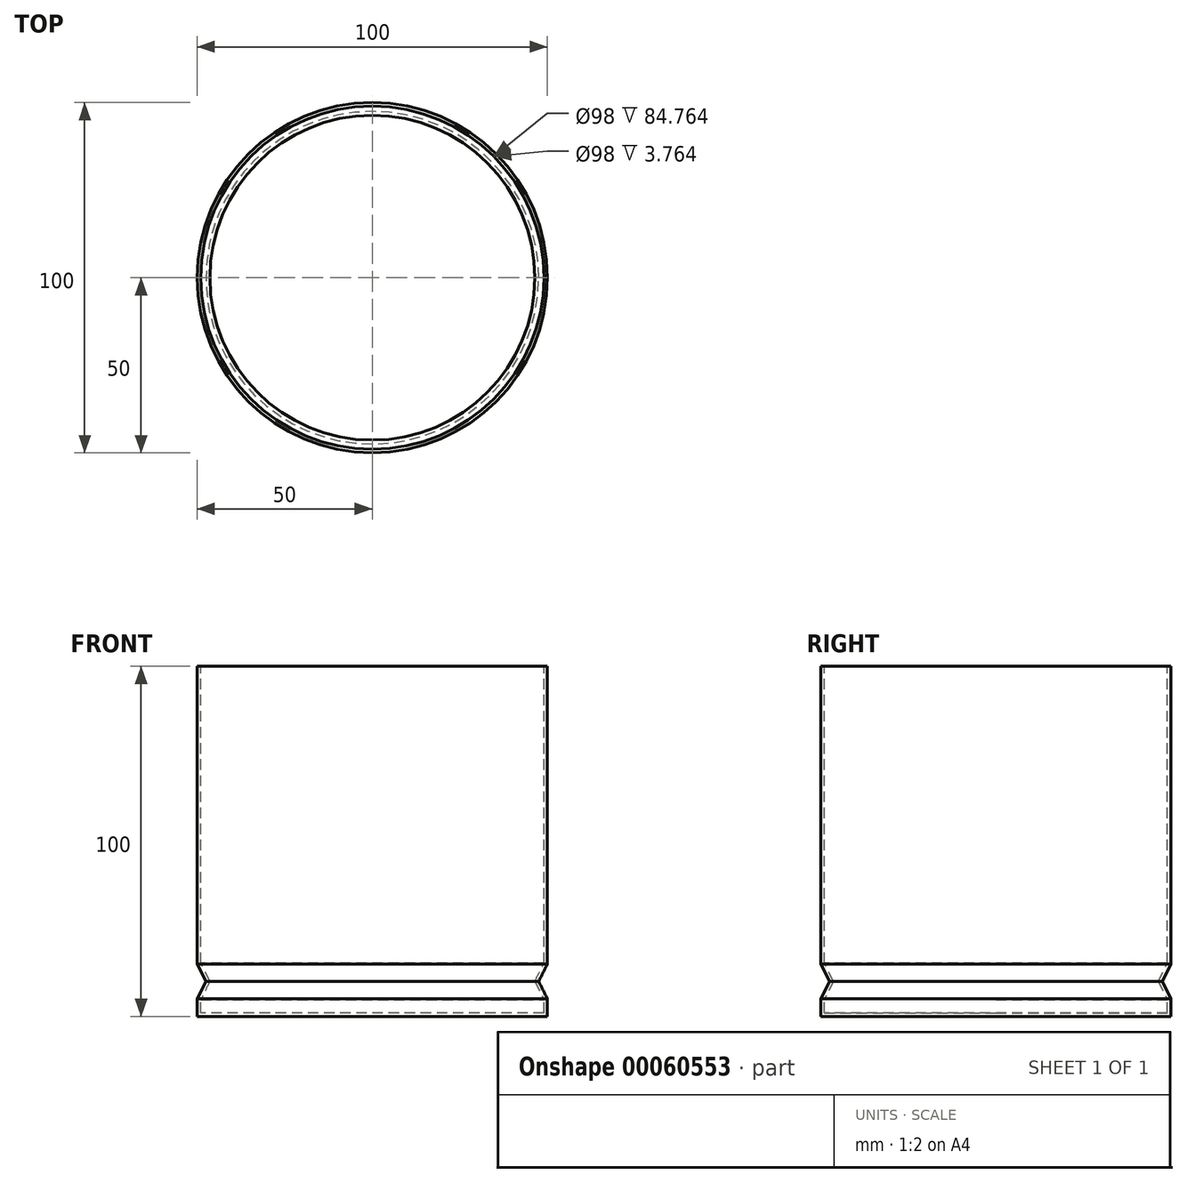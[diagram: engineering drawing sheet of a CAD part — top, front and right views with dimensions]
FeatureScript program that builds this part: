
annotation { "Feature Type Name" : "Feature", "Feature Type Description" : "" }
export const myFeature = defineFeature(function(context is Context, id is Id, definition is map)
    precondition{}
    {
        {
            var Q0;
            Q0=qCreatedBy(makeId("Top.planeOp"),FACE);
            cPlane(context, id + "F0", {"entities" : qUnion([Q0]), "cplaneType" : CPlaneType.OFFSET, "offset" : 50 * mm, "width" : 150 * mm, "height" : 150 * mm});
        }
        {
            var Q0;
            Q0=qCreatedBy(makeId("Top.planeOp"),FACE);
            cPlane(context, id + "F1", {"entities" : qUnion([Q0]), "cplaneType" : CPlaneType.OFFSET, "offset" : 35 * mm, "oppositeDirection" : true, "width" : 150 * mm, "height" : 150 * mm});
        }
        {
            var Q0;
            Q0=qCreatedBy(makeId("Top.planeOp"),FACE);
            cPlane(context, id + "F2", {"entities" : qUnion([Q0]), "cplaneType" : CPlaneType.OFFSET, "offset" : 40 * mm, "oppositeDirection" : true, "width" : 150 * mm, "height" : 150 * mm});
        }
        {
            var Q0;
            Q0=qCreatedBy(makeId("Top.planeOp"),FACE);
            cPlane(context, id + "F3", {"entities" : qUnion([Q0]), "cplaneType" : CPlaneType.OFFSET, "offset" : 45 * mm, "oppositeDirection" : true, "width" : 150 * mm, "height" : 150 * mm});
        }
        {
            var Q0;
            Q0=qCreatedBy(makeId("Top.planeOp"),FACE);
            cPlane(context, id + "F4", {"entities" : qUnion([Q0]), "cplaneType" : CPlaneType.OFFSET, "offset" : 50 * mm, "oppositeDirection" : true, "width" : 150 * mm, "height" : 150 * mm});
        }
        {
            var Q0;
            Q0=qCreatedBy(id+"F0.planeOp",FACE);
            var sketch = newSketch(context, id + "F5", { "sketchPlane" : qUnion([Q0])});
            skCircle(sketch, "E0", {"center": v(0, 0) * mm, "radius": 50 * mm});
            skSolve(sketch);
        }
        {
            var Q0;
            Q0=qCreatedBy(id+"F4.planeOp",FACE);
            var sketch = newSketch(context, id + "F6", { "sketchPlane" : qUnion([Q0])});
            skPoint(sketch, "E1.rect.middle", {"position": v(0, 0) * mm});
            skPoint(sketch, "E2.visualSharp", {"position": v(-35.36, 35.36) * mm});
            skPoint(sketch, "E3.visualSharp", {"position": v(35.36, 35.36) * mm});
            skPoint(sketch, "E4.visualSharp", {"position": v(35.36, -35.36) * mm});
            skPoint(sketch, "E5.visualSharp", {"position": v(-35.36, -35.36) * mm});
            skCircle(sketch, "E6", {"center": v(0, 0) * mm, "radius": 50 * mm});
            skSolve(sketch);
        }
        {
            var Q0;
            Q0=qCreatedBy(id+"F3.planeOp",FACE);
            var sketch = newSketch(context, id + "F7", { "sketchPlane" : qUnion([Q0])});
            skCircle(sketch, "E7", {"center": v(0, 0) * mm, "radius": 50 * mm});
            skSolve(sketch);
        }
        {
            var Q0;
            Q0=qCreatedBy(id+"F2.planeOp",FACE);
            var sketch = newSketch(context, id + "F8", { "sketchPlane" : qUnion([Q0])});
            skCircle(sketch, "E8", {"center": v(0, 0) * mm, "radius": 47.5 * mm});
            skSolve(sketch);
        }
        {
            var Q0;
            Q0=qCreatedBy(id+"F1.planeOp",FACE);
            var sketch = newSketch(context, id + "F9", { "sketchPlane" : qUnion([Q0])});
            skCircle(sketch, "E9", {"center": v(0, 0) * mm, "radius": 50 * mm});
            skSolve(sketch);
        }
        {
            var Q0;
            Q0=makeQuery(id+"F5.imprint","IMPRINT",FACE,{"disambiguationData":[TD([[makeQuery(id+"F5.imprint","IMPRINT",EDGE,{"derivedFrom":sQuery(id+"F5.wireOp",EDGE,"E0")}),1.0]])]});
            var Q1;
            Q1=makeQuery(id+"F9.imprint","IMPRINT",FACE,{"disambiguationData":[TD([[makeQuery(id+"F9.imprint","IMPRINT",EDGE,{"derivedFrom":sQuery(id+"F9.wireOp",EDGE,"E9")}),1.0]])]});
            loft(context, id + "F10", {"sheetProfilesArray" : [{ "sheetProfileEntities" : qUnion([Q0]) }, { "sheetProfileEntities" : qUnion([Q1]) }]});
        }
        {
            var Q1;
            Q1=makeQuery(id+"F10.opLoft","CAP_FACE",FACE,{"disambiguationData":[OSD([makeQuery(id+"F9.imprint","IMPRINT",FACE,{"disambiguationData":[TD([[makeQuery(id+"F9.imprint","IMPRINT",EDGE,{"derivedFrom":sQuery(id+"F9.wireOp",EDGE,"E9")}),1.0]])]})])],"isStart":true});
            var Q2;
            Q2=makeQuery(id+"F8.imprint","IMPRINT",FACE,{"disambiguationData":[TD([[makeQuery(id+"F8.imprint","IMPRINT",EDGE,{"derivedFrom":sQuery(id+"F8.wireOp",EDGE,"E8")}),1.0]])]});
            loft(context, id + "F11", {"operationType" : NewBodyOperationType.ADD, "sheetProfilesArray" : [{ "sheetProfileEntities" : qUnion([Q1]) }, { "sheetProfileEntities" : qUnion([Q2]) }]});
        }
        {
            var Q1;
            Q1=makeQuery(id+"F11.opLoft","CAP_FACE",FACE,{"disambiguationData":[OSD([makeQuery(id+"F8.imprint","IMPRINT",FACE,{"disambiguationData":[TD([[makeQuery(id+"F8.imprint","IMPRINT",EDGE,{"derivedFrom":sQuery(id+"F8.wireOp",EDGE,"E8")}),1.0]])]})])],"isStart":true});
            var Q2;
            Q2=makeQuery(id+"F7.imprint","IMPRINT",FACE,{"disambiguationData":[TD([[makeQuery(id+"F7.imprint","IMPRINT",EDGE,{"derivedFrom":sQuery(id+"F7.wireOp",EDGE,"E7")}),1.0]])]});
            loft(context, id + "F12", {"operationType" : NewBodyOperationType.ADD, "sheetProfilesArray" : [{ "sheetProfileEntities" : qUnion([Q1]) }, { "sheetProfileEntities" : qUnion([Q2]) }]});
        }
        {
            var Q1;
            Q1=makeQuery(id+"F12.opLoft","CAP_FACE",FACE,{"disambiguationData":[OSD([makeQuery(id+"F7.imprint","IMPRINT",FACE,{"disambiguationData":[TD([[makeQuery(id+"F7.imprint","IMPRINT",EDGE,{"derivedFrom":sQuery(id+"F7.wireOp",EDGE,"E7")}),1.0]])]})])],"isStart":true});
            var Q2;
            Q2=makeQuery(id+"F6.imprint","IMPRINT",FACE,{"disambiguationData":[TD([[makeQuery(id+"F6.imprint","IMPRINT",EDGE,{"derivedFrom":sQuery(id+"F6.wireOp",EDGE,"E6")}),1.0]])]});
            loft(context, id + "F13", {"operationType" : NewBodyOperationType.ADD, "sheetProfilesArray" : [{ "sheetProfileEntities" : qUnion([Q1]) }, { "sheetProfileEntities" : qUnion([Q2]) }]});
        }
        {
            var Q0;
            Q0=makeQuery(id+"F10.opLoft","CAP_FACE",FACE,{"disambiguationData":[OSD([makeQuery(id+"F5.imprint","IMPRINT",FACE,{"disambiguationData":[TD([[makeQuery(id+"F5.imprint","IMPRINT",EDGE,{"derivedFrom":sQuery(id+"F5.wireOp",EDGE,"E0")}),1.0]])]})])],"isStart":true});
            shell(context, id + "F14", {"entities" : qUnion([Q0]), "thickness" : 1 * mm});
        }
    });
